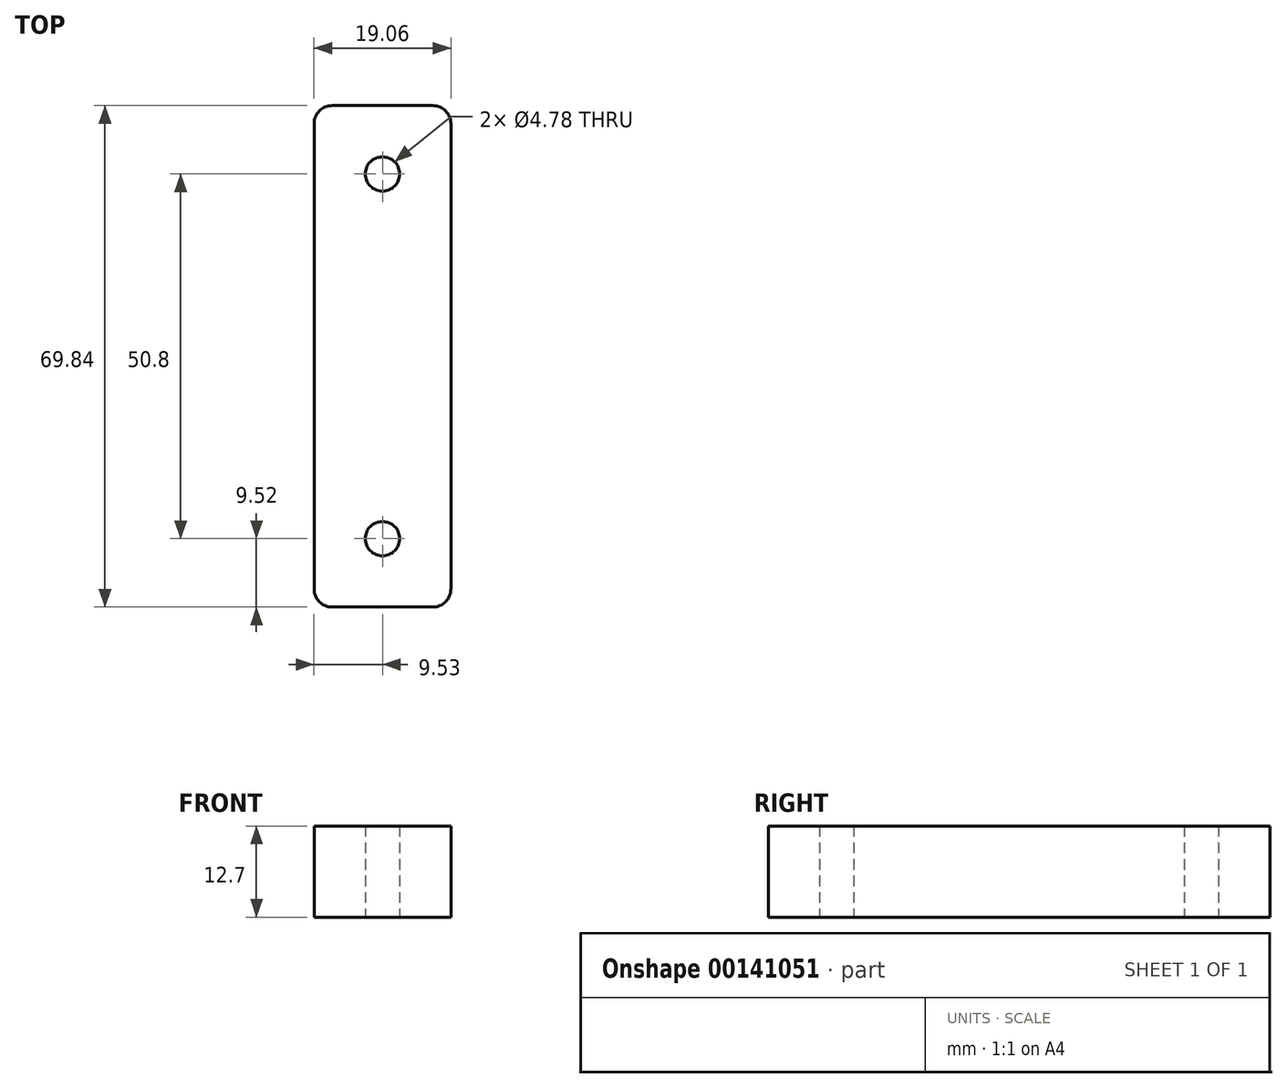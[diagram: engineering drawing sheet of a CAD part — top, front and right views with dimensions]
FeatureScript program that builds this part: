
annotation { "Feature Type Name" : "Feature", "Feature Type Description" : "" }
export const myFeature = defineFeature(function(context is Context, id is Id, definition is map)
    precondition{}
    {
        {
            var Q0;
            Q0=qCreatedBy(makeId("Top.planeOp"),FACE);
            var sketch = newSketch(context, id + "F0", { "sketchPlane" : qUnion([Q0])});
            skLineSegment(sketch, "E0.bottom", {"start": v(9.53, -34.93) * mm, "end": v(-9.53, -34.93) * mm});
            skLineSegment(sketch, "E0.top", {"start": v(9.53, 34.93) * mm, "end": v(-9.52, 34.93) * mm});
            skLineSegment(sketch, "E0.left", {"start": v(9.53, -34.93) * mm, "end": v(9.53, 34.93) * mm});
            skLineSegment(sketch, "E0.right", {"start": v(-9.53, -34.93) * mm, "end": v(-9.52, 34.93) * mm});
            skPoint(sketch, "E0.middle", {"position": v(0, 0) * mm});
            skCircle(sketch, "E1", {"center": v(0, 25.4) * mm, "radius": 2.39 * mm});
            skCircle(sketch, "E2", {"center": v(0, -25.4) * mm, "radius": 2.39 * mm});
            skSolve(sketch);
        }
        {
            var Q0;
            Q0 = qSketchRegion(id + "F0", true);
            extrude(context, id + "F1", {"entities" : qUnion([Q0]), "depth" : 12.7 * mm});
        }
        {
            var Q0;
            Q0=makeQuery(id+"F1.opExtrude","SWEPT_EDGE",EDGE,{"disambiguationData":[OSD([sQuery(id+"F0.wireOp",EDGE,"E0.bottom"),sQuery(id+"F0.wireOp",EDGE,"E0.left")])]});
            var Q1;
            Q1=makeQuery(id+"F1.opExtrude","SWEPT_EDGE",EDGE,{"disambiguationData":[OSD([sQuery(id+"F0.wireOp",EDGE,"E0.bottom"),sQuery(id+"F0.wireOp",EDGE,"E0.right")])]});
            var Q2;
            Q2=makeQuery(id+"F1.opExtrude","SWEPT_EDGE",EDGE,{"disambiguationData":[OSD([sQuery(id+"F0.wireOp",EDGE,"E0.top"),sQuery(id+"F0.wireOp",EDGE,"E0.left")])]});
            var Q3;
            Q3=makeQuery(id+"F1.opExtrude","SWEPT_EDGE",EDGE,{"disambiguationData":[OSD([sQuery(id+"F0.wireOp",EDGE,"E0.top"),sQuery(id+"F0.wireOp",EDGE,"E0.right")])]});
            fillet(context, id + "F2", {"entities" : qUnion([Q0, Q1, Q2, Q3]), "radius" : 2.54 * mm, "tangentPropagation" : true, "allowEdgeOverflow" : false});
        }
    });
